# Revit family: Trane_TVR_Indoor_Medium static pressure_4TVD0048EF000AA(2nd DC)
name_source: partatom
category: Equipamento mecânico
units: mm (PartAtom-declared; Revit-internal decimal feet)

## family parameters
Com base no plano de trabalho = Não
Compartilhado = Não
Corte com vazios quando carregada = Não
Cota do conector redondo = Utilizar diâmetro
Número OmniClass = 23.75.00.00
Ponto de cálculo do ambiente = Não
Sempre na vertical = Sim
Tipo de parte = Normal
Título OmniClass = Climate Control (HVAC)

## types (1)
- 4TVD0048EF000AA
    Air  Flow = 1960/1860/1760/1660/1560/1460/1360
    Condensation = air
    Cooling Capacity = 14.00 kW
    Cooling Power Input = 250 W
    Depth = 865  [stored 2.83793 ft]
    Descrição = High efficiency air cooled
    Fabricante = Trane
    Gas = R410a
    Gas pipe = 15.9  [stored 0.0521654 ft]
    Heating Capacity = 15.50 kW
    Heating Power Input = 250 W
    Height = 300
    Installation = Indoor installation
    Liquid pipe = 9.53
    Machine material = grilles：ABS/HIPS
    Maximum Fuse Amps = 15 A
    Minimum Circuit Amps = 3 A
    Modelo = 4TVD0048EF000AA
    Net Weight = 46.50 kg
    Power supply = 220-240V ~50/60Hz
    Series = TVR ULTRA
    URL = https://www.trane.com
    Width = 1290
    clearance access behind = 0  [stored 0 ft]
    clearance access front = 0  [stored 0 ft]
    clearance access left = 590
    clearance access right = 600

note: [stored X ft] marks values corroborated as IEEE doubles in the binary element streams (Revit-internal decimal feet)

## geometry (parser evidence)
native form markers: Sweep x4
no freeform markers — native parametric forms only
